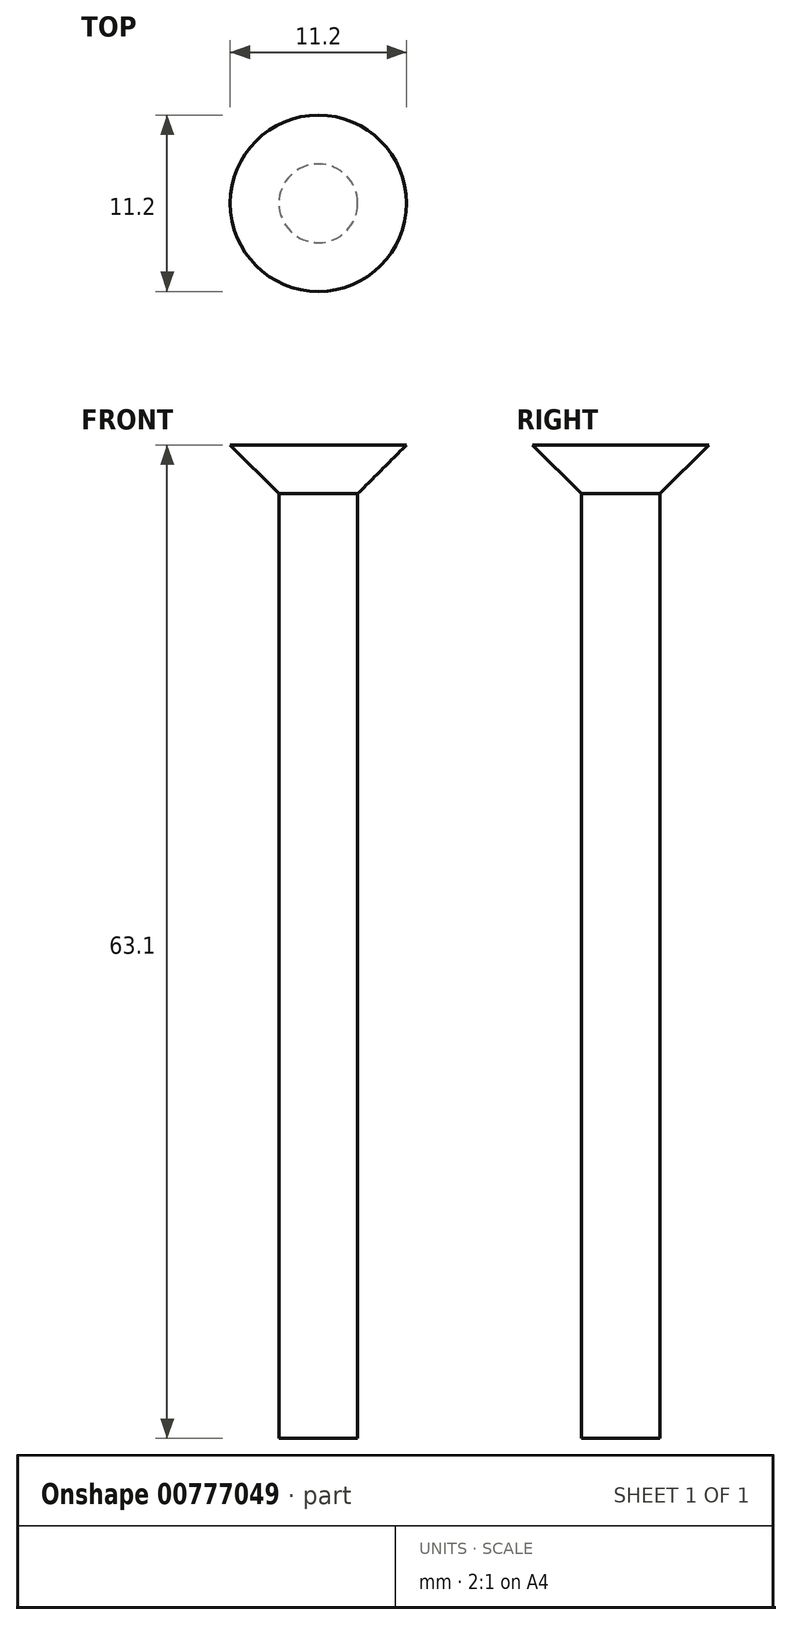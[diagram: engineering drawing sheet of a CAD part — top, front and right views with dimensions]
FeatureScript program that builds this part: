
annotation { "Feature Type Name" : "Feature", "Feature Type Description" : "" }
export const myFeature = defineFeature(function(context is Context, id is Id, definition is map)
    precondition{}
    {
        {
            var Q0;
            Q0=qCreatedBy(makeId("Top.planeOp"),FACE);
            var sketch = newSketch(context, id + "F0", { "sketchPlane" : qUnion([Q0])});
            skCircle(sketch, "E0", {"center": v(0, 0) * mm, "radius": 2.5 * mm});
            skSolve(sketch);
        }
        {
            var Q0;
            Q0=qSketchRegion(id+"F0",true);
            extrude(context, id + "F1", {"entities" : qUnion([Q0]), "depth" : 60 * mm});
        }
        {
            var Q0;
            Q0=makeQuery(id+"F1.opExtrude","CAP_FACE",FACE,{"disambiguationData":[OSD([sQuery(id+"F0.wireOp",EDGE,"E0")])],"isStart":false});
            var sketch = newSketch(context, id + "F2", { "sketchPlane" : qUnion([Q0])});
            skCircle(sketch, "E1", {"center": v(0, 0) * mm, "radius": 5.6 * mm});
            skSolve(sketch);
        }
        {
            var Q0;
            Q0=qSketchRegion(id+"F2",true);
            extrude(context, id + "F3", {"entities" : qUnion([Q0]), "operationType" : NewBodyOperationType.ADD, "depth" : 3.1 * mm});
        }
        {
            var Q0;
            Q0=makeQuery(id+"F3.opExtrude","CAP_EDGE",EDGE,{"disambiguationData":[OSD([sQuery(id+"F2.wireOp",EDGE,"E1")])],"isStart":true});
            chamfer(context, id + "F4", {"entities" : qUnion([Q0]), "width" : 3.1 * mm, "tangentPropagation" : true});
        }
    });
